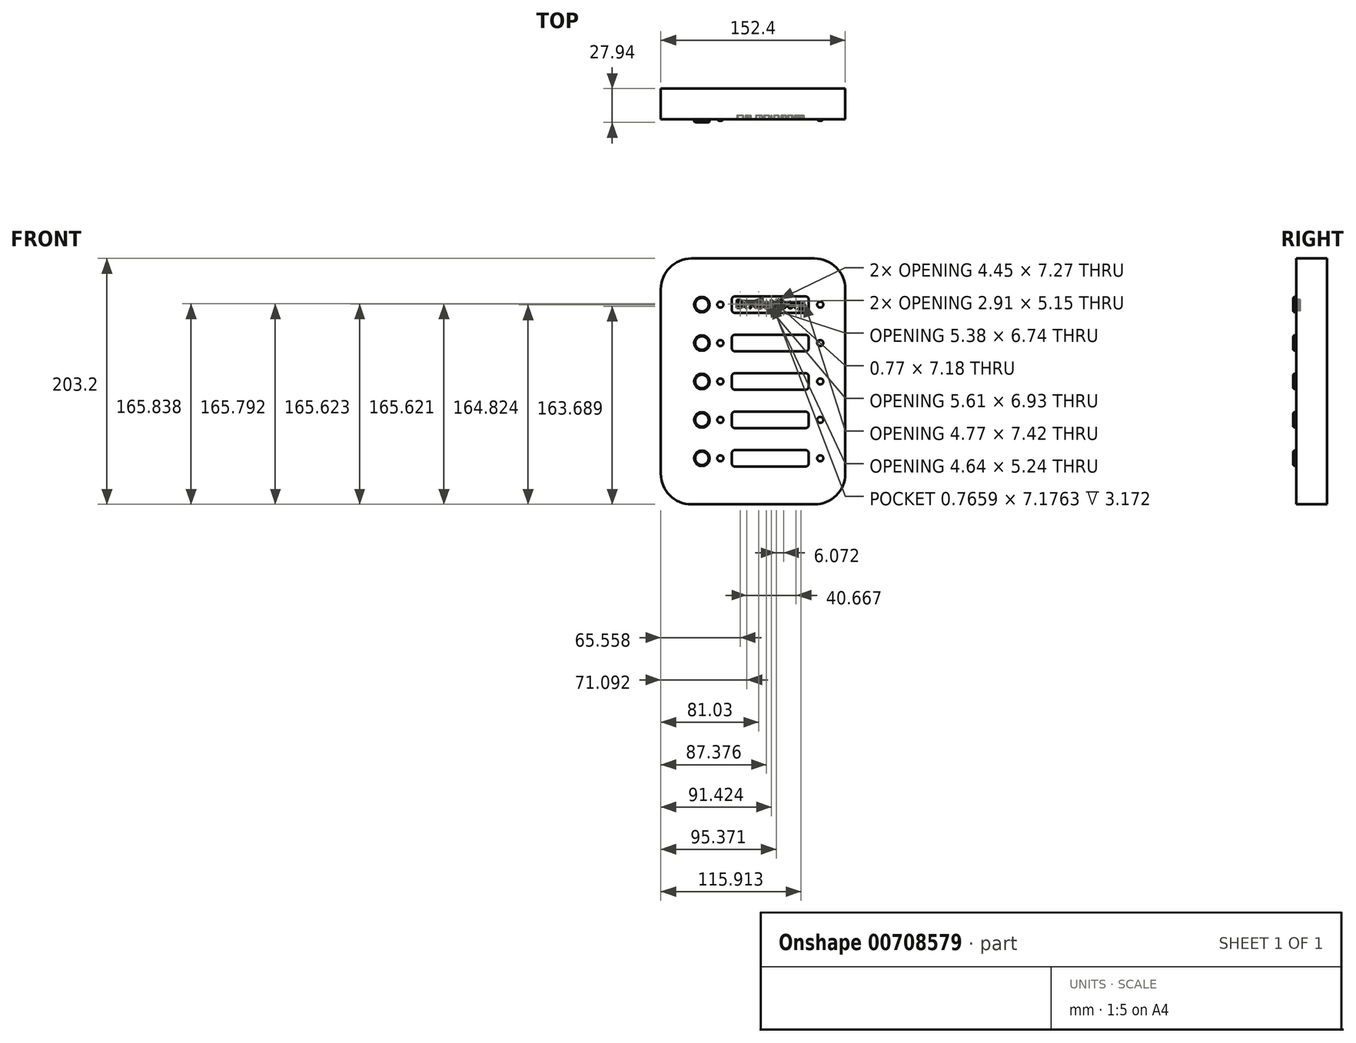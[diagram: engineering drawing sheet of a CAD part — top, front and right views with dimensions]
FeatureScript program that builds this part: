
annotation { "Feature Type Name" : "Feature", "Feature Type Description" : "" }
export const myFeature = defineFeature(function(context is Context, id is Id, definition is map)
    precondition{}
    {
        {
            var Q0;
            Q0=qCreatedBy(makeId("Front.planeOp"),FACE);
            var sketch = newSketch(context, id + "F0", { "sketchPlane" : qUnion([Q0])});
            skLineSegment(sketch, "E0.bottom", {"start": v(50.8, -101.6) * mm, "end": v(-50.8, -101.6) * mm});
            skLineSegment(sketch, "E0.top", {"start": v(50.8, 101.6) * mm, "end": v(-50.8, 101.6) * mm});
            skLineSegment(sketch, "E0.left", {"start": v(76.2, -76.2) * mm, "end": v(76.2, 76.2) * mm});
            skLineSegment(sketch, "E0.right", {"start": v(-76.2, -76.2) * mm, "end": v(-76.2, 76.2) * mm});
            skPoint(sketch, "E0.middle", {"position": v(0, 0) * mm});
            skPoint(sketch, "E1.visualSharp", {"position": v(-76.2, 101.6) * mm});
            skArc(sketch, "E1.filletArc", {"start": v(-50.8, 101.6) * mm, "mid": v(-68.76, 94.16) * mm, "end": v(-76.2, 76.2) * mm});
            skPoint(sketch, "E2.visualSharp", {"position": v(76.2, 101.6) * mm});
            skArc(sketch, "E2.filletArc", {"start": v(76.2, 76.2) * mm, "mid": v(68.76, 94.16) * mm, "end": v(50.8, 101.6) * mm});
            skPoint(sketch, "E3.visualSharp", {"position": v(76.2, -101.6) * mm});
            skArc(sketch, "E3.filletArc", {"start": v(50.8, -101.6) * mm, "mid": v(68.76, -94.16) * mm, "end": v(76.2, -76.2) * mm});
            skPoint(sketch, "E4.visualSharp", {"position": v(-76.2, -101.6) * mm});
            skArc(sketch, "E4.filletArc", {"start": v(-76.2, -76.2) * mm, "mid": v(-68.76, -94.16) * mm, "end": v(-50.8, -101.6) * mm});
            skSolve(sketch);
        }
        {
            var Q0;
            Q0 = qSketchRegion(id + "F0", true);
            extrude(context, id + "F1", {"entities" : qUnion([Q0]), "oppositeDirection" : true, "depth" : 25.4 * mm, "offsetDistance" : 25.4 * mm});
        }
        {
            var Q0;
            Q0=makeQuery(id+"F1.opExtrude","CAP_FACE",FACE,{"disambiguationData":[OSD([sQuery(id+"F0.wireOp",EDGE,"E0.bottom"),sQuery(id+"F0.wireOp",EDGE,"E0.top"),sQuery(id+"F0.wireOp",EDGE,"E0.left"),sQuery(id+"F0.wireOp",EDGE,"E0.right"),sQuery(id+"F0.wireOp",EDGE,"E1.filletArc"),sQuery(id+"F0.wireOp",EDGE,"E2.filletArc"),sQuery(id+"F0.wireOp",EDGE,"E3.filletArc"),sQuery(id+"F0.wireOp",EDGE,"E4.filletArc")])],"isStart":true});
            var sketch = newSketch(context, id + "F2", { "sketchPlane" : qUnion([Q0])});
            skCircle(sketch, "E5", {"center": v(-42.27, 63.5) * mm, "radius": 6.35 * mm});
            skCircle(sketch, "E6.0.1.0", {"center": v(-42.27, 31.75) * mm, "radius": 6.35 * mm});
            skCircle(sketch, "E6.0.2.0", {"center": v(-42.27, 0) * mm, "radius": 6.35 * mm});
            skCircle(sketch, "E6.0.3.0", {"center": v(-42.27, -31.75) * mm, "radius": 6.35 * mm});
            skCircle(sketch, "E6.0.4.0", {"center": v(-42.27, -63.5) * mm, "radius": 6.35 * mm});
            skLineSegment(sketch, "E6.direction1", {"start": v(-42.27, 63.5) * mm, "end": v(-42.27, 63.5) * mm});
            skLineSegment(sketch, "E6.direction2", {"start": v(-42.27, 63.5) * mm, "end": v(-42.27, 31.75) * mm, "construction": true});
            skCircle(sketch, "E7", {"center": v(-27.03, 63.5) * mm, "radius": 2.5 * mm});
            skLineSegment(sketch, "E8.direction1", {"start": v(-27.03, 63.5) * mm, "end": v(-25.46, 63.5) * mm, "construction": true});
            skCircle(sketch, "E9.0.1.0", {"center": v(-27.03, 31.75) * mm, "radius": 2.5 * mm});
            skCircle(sketch, "E9.0.2.0", {"center": v(-27.03, 0) * mm, "radius": 2.5 * mm});
            skCircle(sketch, "E9.0.3.0", {"center": v(-27.03, -31.75) * mm, "radius": 2.5 * mm});
            skCircle(sketch, "E9.0.4.0", {"center": v(-27.03, -63.5) * mm, "radius": 2.5 * mm});
            skCircle(sketch, "E9.1.0.0", {"center": v(55.52, 63.5) * mm, "radius": 2.5 * mm});
            skCircle(sketch, "E9.1.1.0", {"center": v(55.52, 31.75) * mm, "radius": 2.5 * mm});
            skCircle(sketch, "E9.1.2.0", {"center": v(55.52, 0) * mm, "radius": 2.5 * mm});
            skCircle(sketch, "E9.1.3.0", {"center": v(55.52, -31.75) * mm, "radius": 2.5 * mm});
            skCircle(sketch, "E9.1.4.0", {"center": v(55.52, -63.5) * mm, "radius": 2.5 * mm});
            skLineSegment(sketch, "E9.direction1", {"start": v(-27.03, 63.5) * mm, "end": v(55.52, 63.5) * mm, "construction": true});
            skLineSegment(sketch, "E9.direction2", {"start": v(-27.03, 63.5) * mm, "end": v(-27.03, 31.75) * mm, "construction": true});
            skLineSegment(sketch, "E10.bottom", {"start": v(43.54, 56.75) * mm, "end": v(-17.57, 56.75) * mm});
            skLineSegment(sketch, "E10.top", {"start": v(43.54, 70.25) * mm, "end": v(-15.06, 70.25) * mm});
            skLineSegment(sketch, "E10.left", {"start": v(46.05, 59.26) * mm, "end": v(46.05, 67.74) * mm});
            skLineSegment(sketch, "E10.right", {"start": v(-17.57, 59.26) * mm, "end": v(-17.57, 67.74) * mm});
            skPoint(sketch, "E10.middle", {"position": v(14.24, 63.5) * mm});
            skLineSegment(sketch, "E11.0.1.0", {"start": v(46.05, 27.5) * mm, "end": v(46.05, 36) * mm});
            skLineSegment(sketch, "E11.0.1.1", {"start": v(43.54, 25) * mm, "end": v(-15.06, 25) * mm});
            skLineSegment(sketch, "E11.0.1.2", {"start": v(43.54, 38.5) * mm, "end": v(-15.06, 38.5) * mm});
            skLineSegment(sketch, "E11.0.1.3", {"start": v(-17.57, 25) * mm, "end": v(-17.57, 38.5) * mm});
            skLineSegment(sketch, "E11.0.2.0", {"start": v(46.05, -4.24) * mm, "end": v(46.05, 4.24) * mm});
            skLineSegment(sketch, "E11.0.2.1", {"start": v(43.54, -6.75) * mm, "end": v(-15.06, -6.75) * mm});
            skLineSegment(sketch, "E11.0.2.2", {"start": v(43.54, 6.75) * mm, "end": v(-15.06, 6.75) * mm});
            skLineSegment(sketch, "E11.0.2.3", {"start": v(-17.57, -4.24) * mm, "end": v(-17.57, 4.24) * mm});
            skLineSegment(sketch, "E11.0.3.0", {"start": v(46.05, -36) * mm, "end": v(46.05, -27.5) * mm});
            skLineSegment(sketch, "E11.0.3.1", {"start": v(43.54, -38.5) * mm, "end": v(-15.06, -38.5) * mm});
            skLineSegment(sketch, "E11.0.3.2", {"start": v(43.54, -25) * mm, "end": v(-15.06, -25) * mm});
            skLineSegment(sketch, "E11.0.3.3", {"start": v(-17.57, -36) * mm, "end": v(-17.57, -27.5) * mm});
            skLineSegment(sketch, "E11.0.4.0", {"start": v(46.05, -67.74) * mm, "end": v(46.05, -59.26) * mm});
            skLineSegment(sketch, "E11.0.4.1", {"start": v(43.54, -70.25) * mm, "end": v(-15.06, -70.25) * mm});
            skLineSegment(sketch, "E11.0.4.2", {"start": v(43.54, -56.75) * mm, "end": v(-15.06, -56.75) * mm});
            skLineSegment(sketch, "E11.0.4.3", {"start": v(-17.57, -67.74) * mm, "end": v(-17.57, -59.26) * mm});
            skLineSegment(sketch, "E11.direction1", {"start": v(-15.06, 56.75) * mm, "end": v(7.83, 56.75) * mm, "construction": true});
            skLineSegment(sketch, "E11.direction2", {"start": v(-17.57, 36) * mm, "end": v(-17.57, 27.5) * mm, "construction": true});
            skPoint(sketch, "E12.visualSharp", {"position": v(46.05, 70.25) * mm});
            skArc(sketch, "E12.filletArc", {"start": v(46.05, 67.74) * mm, "mid": v(45.31, 69.51) * mm, "end": v(43.54, 70.25) * mm});
            skPoint(sketch, "E13.visualSharp", {"position": v(46.05, 56.75) * mm});
            skArc(sketch, "E13.filletArc", {"start": v(43.54, 56.75) * mm, "mid": v(45.31, 57.49) * mm, "end": v(46.05, 59.26) * mm});
            skPoint(sketch, "E14.visualSharp", {"position": v(-17.57, 70.25) * mm});
            skArc(sketch, "E14.filletArc", {"start": v(-15.06, 70.25) * mm, "mid": v(-16.83, 69.51) * mm, "end": v(-17.57, 67.74) * mm});
            skPoint(sketch, "E15.visualSharp", {"position": v(-17.57, 56.75) * mm});
            skArc(sketch, "E15.filletArc", {"start": v(-17.57, 59.26) * mm, "mid": v(-16.83, 57.49) * mm, "end": v(-15.06, 56.75) * mm});
            skPoint(sketch, "E16.newPointA", {"position": v(-17.57, 38.5) * mm});
            skArc(sketch, "E16.filletArc", {"start": v(-15.06, 38.5) * mm, "mid": v(-16.83, 37.76) * mm, "end": v(-17.57, 36) * mm});
            skPoint(sketch, "E17.visualSharp", {"position": v(-17.57, 25) * mm});
            skArc(sketch, "E17.filletArc", {"start": v(-17.57, 27.5) * mm, "mid": v(-16.83, 25.74) * mm, "end": v(-15.06, 25) * mm});
            skPoint(sketch, "E18.visualSharp", {"position": v(46.05, 38.5) * mm});
            skArc(sketch, "E18.filletArc", {"start": v(46.05, 36) * mm, "mid": v(45.31, 37.76) * mm, "end": v(43.54, 38.5) * mm});
            skPoint(sketch, "E19.visualSharp", {"position": v(46.05, 25) * mm});
            skArc(sketch, "E19.filletArc", {"start": v(43.54, 25) * mm, "mid": v(45.31, 25.74) * mm, "end": v(46.05, 27.5) * mm});
            skPoint(sketch, "E20.visualSharp", {"position": v(46.05, 6.75) * mm});
            skArc(sketch, "E20.filletArc", {"start": v(46.05, 4.24) * mm, "mid": v(45.31, 6.01) * mm, "end": v(43.54, 6.75) * mm});
            skPoint(sketch, "E21.visualSharp", {"position": v(46.05, -6.75) * mm});
            skArc(sketch, "E21.filletArc", {"start": v(43.54, -6.75) * mm, "mid": v(45.31, -6.01) * mm, "end": v(46.05, -4.24) * mm});
            skPoint(sketch, "E22.visualSharp", {"position": v(-17.57, -6.75) * mm});
            skArc(sketch, "E22.filletArc", {"start": v(-17.57, -4.24) * mm, "mid": v(-16.83, -6.01) * mm, "end": v(-15.06, -6.75) * mm});
            skPoint(sketch, "E23.visualSharp", {"position": v(-17.57, 6.75) * mm});
            skArc(sketch, "E23.filletArc", {"start": v(-15.06, 6.75) * mm, "mid": v(-16.83, 6.01) * mm, "end": v(-17.57, 4.24) * mm});
            skPoint(sketch, "E24.visualSharp", {"position": v(-17.57, -25) * mm});
            skArc(sketch, "E24.filletArc", {"start": v(-15.06, -25) * mm, "mid": v(-16.83, -25.74) * mm, "end": v(-17.57, -27.5) * mm});
            skPoint(sketch, "E25.visualSharp", {"position": v(46.05, -25) * mm});
            skArc(sketch, "E25.filletArc", {"start": v(46.05, -27.5) * mm, "mid": v(45.31, -25.74) * mm, "end": v(43.54, -25) * mm});
            skPoint(sketch, "E26.visualSharp", {"position": v(46.05, -38.5) * mm});
            skArc(sketch, "E26.filletArc", {"start": v(43.54, -38.5) * mm, "mid": v(45.31, -37.76) * mm, "end": v(46.05, -36) * mm});
            skPoint(sketch, "E27.visualSharp", {"position": v(-17.57, -38.5) * mm});
            skArc(sketch, "E27.filletArc", {"start": v(-17.57, -36) * mm, "mid": v(-16.83, -37.76) * mm, "end": v(-15.06, -38.5) * mm});
            skPoint(sketch, "E28.visualSharp", {"position": v(-17.57, -56.75) * mm});
            skArc(sketch, "E28.filletArc", {"start": v(-15.06, -56.75) * mm, "mid": v(-16.83, -57.49) * mm, "end": v(-17.57, -59.26) * mm});
            skPoint(sketch, "E29.visualSharp", {"position": v(46.05, -56.75) * mm});
            skArc(sketch, "E29.filletArc", {"start": v(46.05, -59.26) * mm, "mid": v(45.31, -57.49) * mm, "end": v(43.54, -56.75) * mm});
            skPoint(sketch, "E30.visualSharp", {"position": v(46.05, -70.25) * mm});
            skArc(sketch, "E30.filletArc", {"start": v(43.54, -70.25) * mm, "mid": v(45.31, -69.51) * mm, "end": v(46.05, -67.74) * mm});
            skPoint(sketch, "E31.visualSharp", {"position": v(-17.57, -70.25) * mm});
            skArc(sketch, "E31.filletArc", {"start": v(-17.57, -67.74) * mm, "mid": v(-16.83, -69.51) * mm, "end": v(-15.06, -70.25) * mm});
            skSolve(sketch);
        }
        {
            var Q0;
            Q0=makeQuery(id+"F2.imprint","IMPRINT",FACE,{"disambiguationData":[TD([[makeQuery(id+"F2.imprint","IMPRINT",EDGE,{"derivedFrom":sQuery(id+"F2.wireOp",EDGE,"E5")}),1.0]])]});
            var Q1;
            Q1=makeQuery(id+"F2.imprint","IMPRINT",FACE,{"disambiguationData":[TD([[makeQuery(id+"F2.imprint","IMPRINT",EDGE,{"derivedFrom":sQuery(id+"F2.wireOp",EDGE,"E6.0.1.0")}),1.0]])]});
            var Q2;
            Q2=makeQuery(id+"F2.imprint","IMPRINT",FACE,{"disambiguationData":[TD([[makeQuery(id+"F2.imprint","IMPRINT",EDGE,{"derivedFrom":sQuery(id+"F2.wireOp",EDGE,"E6.0.3.0")}),1.0]])]});
            var Q3;
            Q3=makeQuery(id+"F2.imprint","IMPRINT",FACE,{"disambiguationData":[TD([[makeQuery(id+"F2.imprint","IMPRINT",EDGE,{"derivedFrom":sQuery(id+"F2.wireOp",EDGE,"E6.0.4.0")}),1.0]])]});
            var Q4;
            Q4=makeQuery(id+"F2.imprint","IMPRINT",FACE,{"disambiguationData":[TD([[makeQuery(id+"F2.imprint","IMPRINT",EDGE,{"derivedFrom":sQuery(id+"F2.wireOp",EDGE,"E6.0.2.0")}),1.0]])]});
            extrude(context, id + "F3", {"entities" : qUnion([Q0, Q1, Q2, Q3, Q4]), "depth" : 2.54 * mm, "offsetDistance" : 25.4 * mm});
        }
        {
            var Q0;
            Q0=makeQuery(id+"F2.imprint","IMPRINT",FACE,{"disambiguationData":[TD([[makeQuery(id+"F2.imprint","IMPRINT",EDGE,{"derivedFrom":sQuery(id+"F2.wireOp",EDGE,"E7")}),1.0]])]});
            var Q1;
            Q1=makeQuery(id+"F2.imprint","IMPRINT",FACE,{"disambiguationData":[TD([[makeQuery(id+"F2.imprint","IMPRINT",EDGE,{"derivedFrom":sQuery(id+"F2.wireOp",EDGE,"E9.0.1.0")}),1.0]])]});
            var Q2;
            Q2=makeQuery(id+"F2.imprint","IMPRINT",FACE,{"disambiguationData":[TD([[makeQuery(id+"F2.imprint","IMPRINT",EDGE,{"derivedFrom":sQuery(id+"F2.wireOp",EDGE,"E9.0.2.0")}),1.0]])]});
            var Q3;
            Q3=makeQuery(id+"F2.imprint","IMPRINT",FACE,{"disambiguationData":[TD([[makeQuery(id+"F2.imprint","IMPRINT",EDGE,{"derivedFrom":sQuery(id+"F2.wireOp",EDGE,"E9.0.3.0")}),1.0]])]});
            var Q4;
            Q4=makeQuery(id+"F2.imprint","IMPRINT",FACE,{"disambiguationData":[TD([[makeQuery(id+"F2.imprint","IMPRINT",EDGE,{"derivedFrom":sQuery(id+"F2.wireOp",EDGE,"E9.0.4.0")}),1.0]])]});
            var Q5;
            Q5=makeQuery(id+"F2.imprint","IMPRINT",FACE,{"disambiguationData":[TD([[makeQuery(id+"F2.imprint","IMPRINT",EDGE,{"derivedFrom":sQuery(id+"F2.wireOp",EDGE,"E9.1.0.0")}),1.0]])]});
            var Q6;
            Q6=makeQuery(id+"F2.imprint","IMPRINT",FACE,{"disambiguationData":[TD([[makeQuery(id+"F2.imprint","IMPRINT",EDGE,{"derivedFrom":sQuery(id+"F2.wireOp",EDGE,"E9.1.1.0")}),1.0]])]});
            var Q7;
            Q7=makeQuery(id+"F2.imprint","IMPRINT",FACE,{"disambiguationData":[TD([[makeQuery(id+"F2.imprint","IMPRINT",EDGE,{"derivedFrom":sQuery(id+"F2.wireOp",EDGE,"E9.1.2.0")}),1.0]])]});
            var Q8;
            Q8=makeQuery(id+"F2.imprint","IMPRINT",FACE,{"disambiguationData":[TD([[makeQuery(id+"F2.imprint","IMPRINT",EDGE,{"derivedFrom":sQuery(id+"F2.wireOp",EDGE,"E9.1.3.0")}),1.0]])]});
            var Q9;
            Q9=makeQuery(id+"F2.imprint","IMPRINT",FACE,{"disambiguationData":[TD([[makeQuery(id+"F2.imprint","IMPRINT",EDGE,{"derivedFrom":sQuery(id+"F2.wireOp",EDGE,"E9.1.4.0")}),1.0]])]});
            var Q10;
            Q10=sQuery(id+"F2.wireOp",EDGE,"E7");
            var Q11;
            Q11=sQuery(id+"F2.wireOp",EDGE,"E8.0.1.0");
            var Q12;
            Q12=sQuery(id+"F2.wireOp",EDGE,"E8.0.2.0");
            var Q13;
            Q13=sQuery(id+"F2.wireOp",EDGE,"E8.0.3.0");
            var Q14;
            Q14=sQuery(id+"F2.wireOp",EDGE,"E8.0.4.0");
            extrude(context, id + "F4", {"entities" : qUnion([Q0, Q1, Q2, Q3, Q4, Q5, Q6, Q7, Q8, Q9]), "surfaceEntities" : qUnion([Q10, Q11, Q12, Q13, Q14]), "depth" : 1.27 * mm, "offsetDistance" : 25.4 * mm});
        }
        {
            var Q0;
            Q0=makeQuery(id+"F4.opExtrude","CAP_EDGE",EDGE,{"disambiguationData":[OSD([sQuery(id+"F2.wireOp",EDGE,"E7")])],"isStart":false});
            var Q1;
            Q1=makeQuery(id+"F4.opExtrude","CAP_EDGE",EDGE,{"disambiguationData":[OSD([sQuery(id+"F2.wireOp",EDGE,"E9.0.1.0")])],"isStart":false});
            var Q2;
            Q2=makeQuery(id+"F4.opExtrude","CAP_EDGE",EDGE,{"disambiguationData":[OSD([sQuery(id+"F2.wireOp",EDGE,"E9.0.2.0")])],"isStart":false});
            var Q3;
            Q3=makeQuery(id+"F4.opExtrude","CAP_EDGE",EDGE,{"disambiguationData":[OSD([sQuery(id+"F2.wireOp",EDGE,"E9.0.3.0")])],"isStart":false});
            var Q4;
            Q4=makeQuery(id+"F4.opExtrude","CAP_EDGE",EDGE,{"disambiguationData":[OSD([sQuery(id+"F2.wireOp",EDGE,"E9.0.4.0")])],"isStart":false});
            var Q5;
            Q5=makeQuery(id+"F4.opExtrude","CAP_EDGE",EDGE,{"disambiguationData":[OSD([sQuery(id+"F2.wireOp",EDGE,"E9.1.4.0")])],"isStart":false});
            var Q6;
            Q6=makeQuery(id+"F4.opExtrude","CAP_EDGE",EDGE,{"disambiguationData":[OSD([sQuery(id+"F2.wireOp",EDGE,"E9.1.3.0")])],"isStart":false});
            var Q7;
            Q7=makeQuery(id+"F4.opExtrude","CAP_EDGE",EDGE,{"disambiguationData":[OSD([sQuery(id+"F2.wireOp",EDGE,"E9.1.2.0")])],"isStart":false});
            var Q8;
            Q8=makeQuery(id+"F4.opExtrude","CAP_EDGE",EDGE,{"disambiguationData":[OSD([sQuery(id+"F2.wireOp",EDGE,"E9.1.1.0")])],"isStart":false});
            var Q9;
            Q9=makeQuery(id+"F4.opExtrude","CAP_EDGE",EDGE,{"disambiguationData":[OSD([sQuery(id+"F2.wireOp",EDGE,"E9.1.0.0")])],"isStart":false});
            fillet(context, id + "F5", {"entities" : qUnion([Q0, Q1, Q2, Q3, Q4, Q5, Q6, Q7, Q8, Q9]), "radius" : 2.5 * mm, "allowEdgeOverflow" : false});
        }
        {
            var Q0;
            Q0=makeQuery(id+"F3.opExtrude","CAP_EDGE",EDGE,{"disambiguationData":[OSD([sQuery(id+"F2.wireOp",EDGE,"E5")])],"isStart":false});
            var Q1;
            Q1=makeQuery(id+"F3.opExtrude","CAP_EDGE",EDGE,{"disambiguationData":[OSD([sQuery(id+"F2.wireOp",EDGE,"E6.0.1.0")])],"isStart":false});
            var Q2;
            Q2=makeQuery(id+"F3.opExtrude","CAP_EDGE",EDGE,{"disambiguationData":[OSD([sQuery(id+"F2.wireOp",EDGE,"E6.0.2.0")])],"isStart":false});
            var Q3;
            Q3=makeQuery(id+"F3.opExtrude","CAP_EDGE",EDGE,{"disambiguationData":[OSD([sQuery(id+"F2.wireOp",EDGE,"E6.0.3.0")])],"isStart":false});
            var Q4;
            Q4=makeQuery(id+"F3.opExtrude","CAP_EDGE",EDGE,{"disambiguationData":[OSD([sQuery(id+"F2.wireOp",EDGE,"E6.0.4.0")])],"isStart":false});
            chamfer(context, id + "F6", {"entities" : qUnion([Q0, Q1, Q2, Q3, Q4]), "width" : 0.76 * mm, "tangentPropagation" : true});
        }
        {
            var Q0;
            Q0=makeQuery(id+"F2.imprint","IMPRINT",FACE,{"disambiguationData":[TD([[makeQuery(id+"F2.imprint","IMPRINT",EDGE,{"derivedFrom":sQuery(id+"F2.wireOp",EDGE,"E10.bottom")}),-1.0]])]});
            var Q1;
            Q1=makeQuery(id+"F2.imprint","IMPRINT",FACE,{"disambiguationData":[TD([[makeQuery(id+"F2.imprint","IMPRINT",EDGE,{"derivedFrom":sQuery(id+"F2.wireOp",EDGE,"E11.0.1.0")}),1.0]])]});
            var Q2;
            Q2=makeQuery(id+"F2.imprint","IMPRINT",FACE,{"disambiguationData":[TD([[makeQuery(id+"F2.imprint","IMPRINT",EDGE,{"derivedFrom":sQuery(id+"F2.wireOp",EDGE,"E11.0.4.0")}),1.0]])]});
            var Q3;
            Q3=makeQuery(id+"F2.imprint","IMPRINT",FACE,{"disambiguationData":[TD([[makeQuery(id+"F2.imprint","IMPRINT",EDGE,{"derivedFrom":sQuery(id+"F2.wireOp",EDGE,"E11.0.3.0")}),1.0]])]});
            var Q4;
            Q4=makeQuery(id+"F2.imprint","IMPRINT",FACE,{"disambiguationData":[TD([[makeQuery(id+"F2.imprint","IMPRINT",EDGE,{"derivedFrom":sQuery(id+"F2.wireOp",EDGE,"E11.0.2.0")}),1.0]])]});
            extrude(context, id + "F7", {"entities" : qUnion([Q0, Q1, Q2, Q3, Q4]), "depth" : 1 / 406.4 * mm, "offsetDistance" : 25.4 * mm});
        }
        {
            var Q0;
            Q0=makeQuery(id+"F7.opExtrude","CAP_FACE",FACE,{"disambiguationData":[OSD([sQuery(id+"F2.wireOp",EDGE,"E10.bottom"),sQuery(id+"F2.wireOp",EDGE,"E10.top"),sQuery(id+"F2.wireOp",EDGE,"E10.left"),sQuery(id+"F2.wireOp",EDGE,"E10.right")])],"isStart":false});
            var sketch = newSketch(context, id + "F8", { "sketchPlane" : qUnion([Q0])});
            skText(sketch, "E32", { "text": "Dr. Goldberg", "fontName": "OpenSans-Regular.ttf"});
            skPoint(sketch, "E33", {"position": v(14.24, 70.25) * mm});
            const initialGuessF8  = {"E32": [-0.01426, 0.06065, 1, 0, 0.0068]};
            skSetInitialGuess(sketch, initialGuessF8);
            skSolve(sketch);
        }
        {
            var Q0;
            Q0 = qSketchRegion(id + "F8", true);
            extrude(context, id + "F9", {"entities" : qUnion([Q0]), "operationType" : NewBodyOperationType.REMOVE, "oppositeDirection" : true, "depth" : 3.17 * mm, "offsetDistance" : 25.4 * mm});
        }
    });
